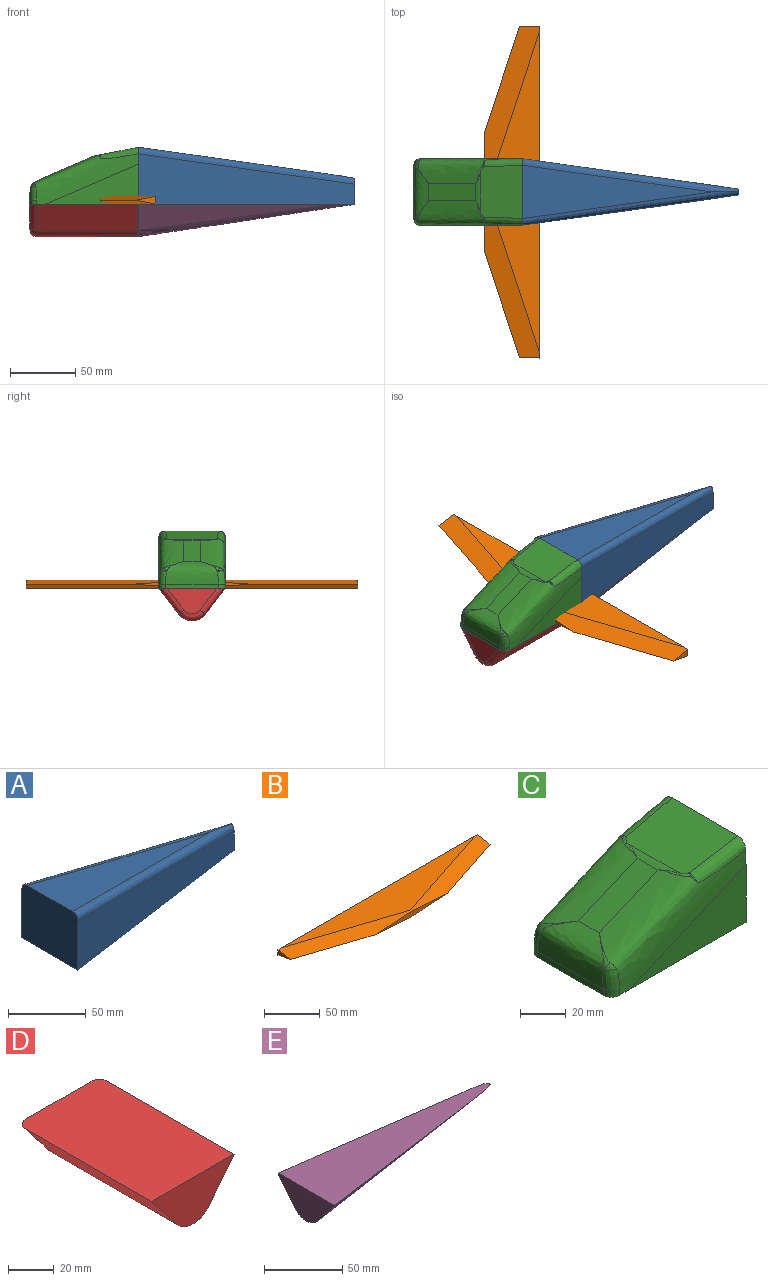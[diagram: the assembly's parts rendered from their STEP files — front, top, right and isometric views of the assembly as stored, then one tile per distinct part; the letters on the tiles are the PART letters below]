
ASSEMBLY  parts=5 mates=4
PART A: 8 faces, bbox 183x52.1x44.9 mm
  f0: plane 50.8x43.69mm, normal (-1,0,0), area 2210.9mm2, adj f1,f3,f4,f5,f6,f7
  f1: plane 165.1x38.66mm, normal (0.14,-0.99,0), area 4510.8mm2, adj f0,f2,f5,f6
  f2: plane 19.91x4.39mm, normal (1,0,0), area 82.5mm2, adj f1,f3,f5,f6,f7
  f3: plane 165.1x38.66mm, normal (0.14,0.99,0), area 4510.8mm2, adj f0,f2,f5,f7
  f4: plane 144.94x40.74mm, normal (0.14,0,0.99), area 2981.3mm2, adj f0,f6,f7
  f5: plane 165.1x50.8mm, normal (0,0,-1), area 4556.2mm2, adj f0,f1,f2,f3
  f6: bspline ~183.04x30.66mm, area 1339.2mm2, adj f0,f1,f2,f4,f7
  f7: bspline ~165.77x28.28mm, area 1339.2mm2, adj f0,f2,f3,f4,f6
PART B: 10 faces, bbox 254x42.2x6.4 mm
  f0: plane 254x6.35mm, normal (0,1,0), area 1610.8mm2, adj f1,f3,f4,f5,f6,f7,f8,f9
  f1: plane 15.37x5.84mm, normal (-1,0,0), area 44.9mm2, adj f0,f6,f7
  f2: plane 91.61x5.74mm, normal (0,-1,0), area 263mm2, adj f6,f7,f8,f9
  f3: plane 15.37x5.84mm, normal (1,0,0), area 44.9mm2, adj f0,f8,f9
  f4: plane 245.83x40.56mm, normal (0,0,1), area 4986.1mm2, adj f0,f6,f8
  f5: plane 245.83x40.56mm, normal (0,0,-1), area 4986.1mm2, adj f0,f7,f9
  f6: plane 127x42.17mm, normal (-0.06,-0.19,0.98), area 1809.2mm2, adj f0,f1,f2,f4,f7,f8
  f7: plane 127x42.17mm, normal (-0.06,-0.19,-0.98), area 1809.2mm2, adj f0,f1,f2,f5,f6,f9
  f8: plane 127x42.17mm, normal (0.06,-0.19,0.98), area 1809.2mm2, adj f0,f2,f3,f4,f6,f9
  f9: plane 127x42.17mm, normal (0.06,-0.19,-0.98), area 1809.2mm2, adj f0,f2,f3,f5,f7,f8
PART C: 29 faces, bbox 95.7x57x54.5 mm
  f0: plane 83.27x51.01mm, normal (0,0,-1), area 4208.1mm2, adj f1,f4,f5,f6,f7,f10,f11,f18
  f1: plane 51.88x44.77mm, normal (1,0,0), area 2206.4mm2, adj f0,f2,f5,f6,f7,f10,f21,f26
  f2: plane 40.43x31.71mm, normal (-0.19,0,0.98), area 1280.5mm2, adj f1,f9,f20,f21,f25,f26
  f3: plane 36x15.57mm, normal (-0.4,0,0.92), area 498.1mm2, adj f7,f8,f9,f10
  f4: plane 40.62x3.16mm, normal (-1,0,0), area 128.1mm2, adj f0,f8,f11,f18
  f5: plane 71.31x30.84mm, normal (0,-1,0), area 1099.5mm2, adj f0,f1,f10
  f6: plane 71.31x30.84mm, normal (0,1,0), area 1099.5mm2, adj f0,f1,f7
  f7: bspline ~90.61x53.4mm, area 2066.9mm2, adj f0,f1,f3,f6,f11,f12,f13,f14
  f8: bspline ~55.88x17.49mm, area 686.1mm2, adj f3,f4,f12,f13,f15,f17
  f9: bspline ~55.88x3.86mm, area 92.3mm2, adj f2,f3,f19,f24
  f10: bspline ~90.61x53.4mm, area 2066.9mm2, adj f0,f1,f3,f5,f15,f16,f17,f18
  f11: bspline ~7.39x5.2mm, area 25.7mm2, adj f0,f4,f7,f13
  f12: bspline ~15.43x10.87mm, area 14.7mm2, adj f7,f8,f14
  f13: bspline ~15.09x6mm, area 78.8mm2, adj f7,f8,f11,f14
  f14: bspline ~4.66x4.09mm, area 7.1mm2, adj f7,f12,f13
  f15: bspline ~15.57x10.9mm, area 14.6mm2, adj f8,f10,f16
  f16: bspline ~4.66x4.09mm, area 9.3mm2, adj f10,f15,f17
  f17: bspline ~12.13x5.96mm, area 78.8mm2, adj f8,f10,f16,f18
  f18: bspline ~6.07x5.15mm, area 25.7mm2, adj f0,f4,f10,f17
  f19: bspline ~10.55x3.86mm, area 5mm2, adj f9,f10,f20
  f20: bspline ~6.28x4.23mm, area 7.3mm2, adj f2,f10,f19,f22
  f21: bspline ~37.15x10.37mm, area 215mm2, adj f1,f2,f10,f22,f23
  f22: bspline ~2.18x0.94mm, area 0.7mm2, adj f20,f21,f23
  f23: bspline ~2.63x2.52mm, area 1.1mm2, adj f10,f21,f22
  f24: bspline ~10.55x3.86mm, area 5mm2, adj f7,f9,f25
  f25: bspline ~6.29x4.23mm, area 7.3mm2, adj f2,f7,f24,f27
  f26: bspline ~30.62x9.08mm, area 215mm2, adj f1,f2,f7,f27,f28
  f27: bspline ~2.18x0.94mm, area 0.7mm2, adj f25,f26,f28
  f28: bspline ~2.63x2.53mm, area 1.1mm2, adj f7,f26,f27
PART D: 9 faces, bbox 54.3x85x30.8 mm
  f0: plane 77.98x19.8mm, normal (-0.79,0,-0.61), area 1954.5mm2, adj f2,f3,f5,f8
  f1: plane 77.98x19.8mm, normal (0.79,0,-0.61), area 1954.5mm2, adj f2,f3,f5,f6
  f2: plane 85.03x52.77mm, normal (0,0,1), area 4208.5mm2, adj f0,f1,f3,f4,f6,f8
  f3: plane 50.8x24.72mm, normal (0,-1,0), area 770.5mm2, adj f0,f1,f2,f5
  f4: plane 37.95x19.65mm, normal (0,1,0), area 441.8mm2, adj f2,f6,f7,f8
  f5: cylinder r=12.7mm len=77.98mm, axis (0,-1,0), area 1804.1mm2, adj f0,f1,f3,f7
  f6: bspline ~23.91x20.15mm, area 190.4mm2, adj f1,f2,f4,f7
  f7: bspline ~20.07x8.03mm, area 164.7mm2, adj f4,f5,f6,f8
  f8: bspline ~23.91x20.15mm, area 190.4mm2, adj f0,f2,f4,f7
PART E: 6 faces, bbox 174.1x50.8x35.4 mm
  f0: plane 151.03x20.94mm, normal (0.11,-0.79,-0.61), area 1921.4mm2, adj f2,f4,f5
  f1: plane 151.03x20.94mm, normal (0.11,0.79,-0.61), area 1921.4mm2, adj f2,f4,f5
  f2: plane 165.1x50.8mm, normal (0,0,1), area 4598.1mm2, adj f0,f1,f3,f4,f5
  f3: plane 1.8x0.11mm, normal (1,0,0), area 0.1mm2, adj f2,f5
  f4: plane 50.8x24.84mm, normal (-1,0,0), area 772.2mm2, adj f0,f1,f2,f5
  f5: bspline ~174.07x35.38mm, area 2620.6mm2, adj f0,f1,f2,f3,f4
PLACE A rot(axis=(0,0,1),0deg) t=(167.52,30.43,0.34)mm
PLACE B rot(axis=(0,0,-1),90deg) t=(61.6,38.1,0.34)mm
PLACE C rot(axis=(0,0,1),0deg) t=(48.43,38.1,0.38)mm
PLACE D rot(axis=(0,0,1),90deg) t=(6.9,38.1,-32.35)mm
PLACE E rot(axis=(0,0,1),0deg) t=(130.63,38.1,-7.84)mm
MATE fastened A.f0 <-> C.f1  axis (-1,0,0) through (48.43,38.1,22.11)mm
MATE fastened B.f5 <-> E.f2  axis (0,0,-1) through (48.08,38.1,0.34)mm
MATE fastened C.f0 <-> D.f2  axis (0,0,-1) through (7,38.1,0.38)mm
MATE fastened E.f2 <-> A.f5  axis (0,0,1) through (107.84,38.1,0.34)mm
